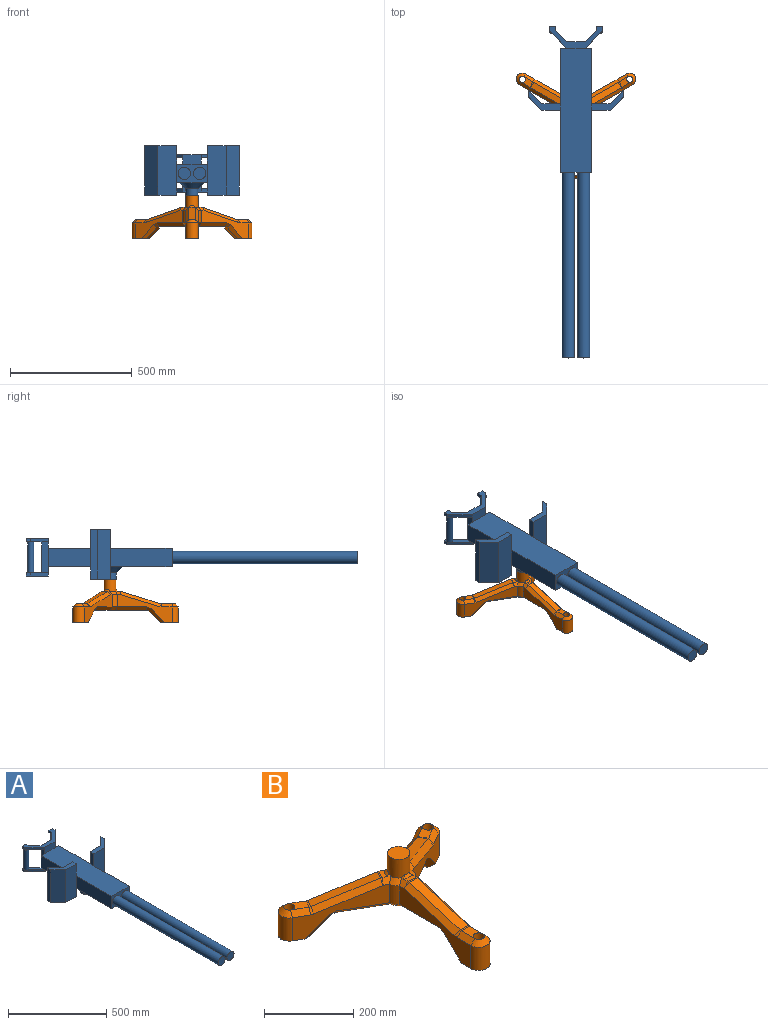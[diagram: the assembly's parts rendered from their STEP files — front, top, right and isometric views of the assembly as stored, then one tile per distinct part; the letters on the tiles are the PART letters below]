
ASSEMBLY  parts=2 mates=1
PART A: 75 faces, bbox 387.2x1360.9x203.2 mm
  f0: cylinder r=25.4mm len=50.8mm, axis (0,0,-1), area 4053.7mm2, adj f18,f74
  f1: plane 71.84x59.14mm, normal (0,0,-1), area 1294.9mm2, adj f3,f44,f45,f57
  f2: plane 71.84x59.14mm, normal (0,0,-1), area 1294.9mm2, adj f4,f42,f43,f54
  f3: plane 127x25.4mm, normal (-1,0,0), area 3225.8mm2, adj f1,f5,f37,f40,f41,f49
  f4: plane 127x25.4mm, normal (1,0,0), area 3225.8mm2, adj f2,f11,f37,f40,f41,f46
  f5: plane 76.2x25.4mm, normal (0,1,0), area 1935.5mm2, adj f3,f6,f7,f8
  f6: plane 508x127mm, normal (0,0,-1), area 56408.7mm2, adj f5,f8,f9,f10,f11,f12,f13,f18
  f7: plane 508x127mm, normal (0,0,1), area 64516mm2, adj f5,f8,f9,f10,f11,f12,f13,f23
  f8: plane 228.6x76.2mm, normal (-1,0,0), area 17419.3mm2, adj f5,f6,f7,f22
  f9: plane 228.6x76.2mm, normal (1,0,0), area 17419.3mm2, adj f6,f7,f11,f20
  f10: plane 254x76.2mm, normal (1,0,0), area 19354.8mm2, adj f6,f7,f13,f19
  f11: plane 76.2x25.4mm, normal (0,1,0), area 1935.5mm2, adj f4,f6,f7,f9
  f12: plane 254x76.2mm, normal (-1,0,0), area 19354.8mm2, adj f6,f7,f13,f21
  f13: plane 127x76.2mm, normal (0,-1,0), area 5623.7mm2, adj f6,f7,f10,f12,f14,f16
  f14: cylinder r=25.4mm len=762mm, axis (0,1,0), area 121609.8mm2, adj f13,f15
  f15: plane 50.8x50.8mm, normal (0,-1,0), area 2026.8mm2, adj f14
  f16: cylinder r=25.4mm len=762mm, axis (0,1,0), area 121609.8mm2, adj f13,f17
  f17: plane 50.8x50.8mm, normal (0,-1,0), area 2026.8mm2, adj f16
  f18: cone r=50.8mm half-angle=45deg, axis (0,0,1), area 8599.1mm2, adj f0,f6
  f19: plane 203.2x76.2mm, normal (0,-1,0), area 15483.8mm2, adj f10,f24,f25,f26,f30,f36
  f20: plane 203.2x76.2mm, normal (0,1,0), area 15483.8mm2, adj f9,f24,f25,f26,f29,f36
  f21: plane 203.2x76.2mm, normal (0,-1,0), area 15483.8mm2, adj f12,f23,f27,f28,f34,f35
  f22: plane 203.2x76.2mm, normal (0,1,0), area 15483.8mm2, adj f8,f23,f27,f28,f32,f35
  f23: plane 76.2x25.4mm, normal (1,0,0), area 1935.5mm2, adj f7,f21,f22,f35
  f24: plane 76.2x25.4mm, normal (-1,0,0), area 1935.5mm2, adj f7,f19,f20,f36
  f25: plane 50.8x25.4mm, normal (-1,0,0), area 1290.3mm2, adj f6,f19,f20,f26
  f26: plane 130.08x79.28mm, normal (0,0,-1), area 3304.1mm2, adj f19,f20,f25,f29,f30,f31
  f27: plane 50.8x25.4mm, normal (1,0,0), area 1290.3mm2, adj f6,f21,f22,f28
  f28: plane 130.08x79.28mm, normal (0,0,-1), area 3304.1mm2, adj f21,f22,f27,f32,f33,f34
  f29: plane 203.2x53.88mm, normal (-0.71,0.71,0), area 15483.8mm2, adj f20,f26,f31,f36
  f30: plane 203.2x53.88mm, normal (0.71,-0.71,0), area 15483.8mm2, adj f19,f26,f31,f36
  f31: plane 203.2x25.4mm, normal (1,0,0), area 5161.3mm2, adj f26,f29,f30,f36
  f32: plane 203.2x53.88mm, normal (0.71,0.71,0), area 15483.8mm2, adj f22,f28,f33,f35
  f33: plane 203.2x25.4mm, normal (-1,0,0), area 5161.3mm2, adj f28,f32,f34,f35
  f34: plane 203.2x53.88mm, normal (-0.71,-0.71,0), area 15483.8mm2, adj f21,f28,f33,f35
  f35: plane 130.08x79.28mm, normal (0,0,1), area 3304.1mm2, adj f21,f22,f23,f32,f33,f34
  f36: plane 130.08x79.28mm, normal (0,0,1), area 3304.1mm2, adj f19,f20,f24,f29,f30,f31
  f37: plane 76.2x38.1mm, normal (0,-1,0), area 2903.2mm2, adj f3,f4,f6,f38,f48,f51
  f38: plane 219.88x90.89mm, normal (0,0,-1), area 5907.6mm2, adj f37,f40,f47,f48,f50,f51,f63,f64
  f39: plane 219.88x90.89mm, normal (0,0,1), area 5907.6mm2, adj f40,f41,f42,f43,f44,f45,f59,f60
  f40: plane 152.4x76.2mm, normal (0,1,0), area 11612.9mm2, adj f3,f4,f38,f39,f43,f45,f47,f50
  f41: plane 76.2x38.1mm, normal (0,-1,0), area 2903.2mm2, adj f3,f4,f7,f39,f42,f44
  f42: plane 71.84x71.84mm, normal (0.71,-0.71,0), area 1290.3mm2, adj f2,f39,f41,f52,f70
  f43: plane 46.44x46.44mm, normal (-0.71,0.71,0), area 834.1mm2, adj f2,f39,f40,f72
  f44: plane 71.84x71.84mm, normal (-0.71,-0.71,0), area 1290.3mm2, adj f1,f39,f41,f55,f60
  f45: plane 46.44x46.44mm, normal (0.71,0.71,0), area 834.1mm2, adj f1,f39,f40,f59
  f46: plane 71.84x59.14mm, normal (0,0,1), area 1294.9mm2, adj f4,f47,f48,f54
  f47: plane 46.44x46.44mm, normal (-0.71,0.71,0), area 834.1mm2, adj f38,f40,f46,f66
  f48: plane 71.84x71.84mm, normal (0.71,-0.71,0), area 1290.3mm2, adj f37,f38,f46,f53,f68
  f49: plane 71.84x59.14mm, normal (0,0,1), area 1294.9mm2, adj f3,f50,f51,f57
  f50: plane 46.44x46.44mm, normal (0.71,0.71,0), area 834.1mm2, adj f38,f40,f49,f64
  f51: plane 71.84x71.84mm, normal (-0.71,-0.71,0), area 1290.3mm2, adj f37,f38,f49,f56,f63
  f52: plane 12.7x12.7mm, normal (0,0,1), area 46mm2, adj f42,f54
  f53: plane 12.7x12.7mm, normal (0,0,-1), area 46mm2, adj f48,f54
  f54: cylinder r=12.7mm len=127mm, axis (0,0,-1), area 10134.1mm2, adj f2,f46,f52,f53,f67,f71
  f55: plane 12.7x12.7mm, normal (0,0,1), area 46mm2, adj f44,f57
  f56: plane 12.7x12.7mm, normal (0,0,-1), area 46mm2, adj f51,f57
  f57: cylinder r=12.7mm len=127mm, axis (0,0,-1), area 10134.1mm2, adj f1,f49,f55,f56,f58,f62
  f58: plane 25.4x19.05mm, normal (0,0,-1), area 230.5mm2, adj f57,f59,f60,f61
  f59: plane 19.05x12.7mm, normal (1,0,0), area 241.9mm2, adj f39,f45,f58,f61
  f60: plane 19.05x12.7mm, normal (-1,0,0), area 241.9mm2, adj f39,f44,f58,f61
  f61: plane 25.4x12.7mm, normal (0,1,0), area 322.6mm2, adj f39,f58,f59,f60
  f62: plane 25.4x19.05mm, normal (0,0,1), area 230.5mm2, adj f57,f63,f64,f65
  f63: plane 19.05x12.7mm, normal (-1,0,0), area 241.9mm2, adj f38,f51,f62,f65
  f64: plane 19.05x12.7mm, normal (1,0,0), area 241.9mm2, adj f38,f50,f62,f65
  f65: plane 25.4x12.7mm, normal (0,1,0), area 322.6mm2, adj f38,f62,f63,f64
  f66: plane 19.05x12.7mm, normal (-1,0,0), area 241.9mm2, adj f38,f47,f67,f69
  f67: plane 25.4x19.05mm, normal (0,0,1), area 230.5mm2, adj f54,f66,f68,f69
  f68: plane 19.05x12.7mm, normal (1,0,0), area 241.9mm2, adj f38,f48,f67,f69
  f69: plane 25.4x12.7mm, normal (0,1,0), area 322.6mm2, adj f38,f66,f67,f68
  f70: plane 19.05x12.7mm, normal (1,0,0), area 241.9mm2, adj f39,f42,f71,f73
  f71: plane 25.4x19.05mm, normal (0,0,-1), area 230.5mm2, adj f54,f70,f72,f73
  f72: plane 19.05x12.7mm, normal (-1,0,0), area 241.9mm2, adj f39,f43,f71,f73
  f73: plane 25.4x12.7mm, normal (0,1,0), area 322.6mm2, adj f39,f70,f71,f72
  f74: plane 50.8x50.8mm, normal (0,0,-1), area 2026.8mm2, adj f0
PART B: 102 faces, bbox 490.9x432x178 mm
  f0: cylinder r=25.4mm len=50.8mm, axis (0,0,-1), area 7731.7mm2, adj f57,f63,f69,f77,f79,f81,f82,f86
  f1: plane 28.72x24.34mm, normal (0,0,1), area 296.1mm2, adj f57,f70,f77,f99
  f2: plane 28.72x24.34mm, normal (0,0,1), area 296.1mm2, adj f69,f76,f81,f98
  f3: plane 195.38x114.3mm, normal (-0.5,0.87,0), area 8864.3mm2, adj f11,f12,f14,f38,f39,f41,f53,f54
  f4: plane 195.38x114.3mm, normal (0.5,0.87,0), area 8864.3mm2, adj f9,f14,f18,f27,f31,f33,f56,f62
  f5: plane 195.38x114.3mm, normal (-0.5,-0.87,0), area 8864.3mm2, adj f9,f15,f18,f23,f24,f25,f66,f72
  f6: plane 225.6x114.3mm, normal (-1,0,0), area 8864.3mm2, adj f10,f13,f15,f29,f30,f32,f89,f90
  f7: plane 195.38x114.3mm, normal (0.5,-0.87,0), area 8864.3mm2, adj f11,f12,f16,f44,f45,f46,f60,f65
  f8: plane 225.6x114.3mm, normal (1,0,0), area 8864.3mm2, adj f10,f13,f16,f35,f37,f40,f80,f82
  f9: cylinder r=25.4mm len=63.5mm, axis (0,0,-1), area 5067.1mm2, adj f4,f5,f18,f61
  f10: cylinder r=25.4mm len=63.5mm, axis (0,0,-1), area 5067.1mm2, adj f6,f8,f13,f85
  f11: cylinder r=25.4mm len=63.5mm, axis (0,0,-1), area 5067.1mm2, adj f3,f7,f12,f55
  f12: plane 73.15x62.32mm, normal (0,0,-1), area 2706.9mm2, adj f3,f7,f11,f21,f38,f46,f97
  f13: plane 73.2x50.8mm, normal (0,0,-1), area 2706.9mm2, adj f6,f8,f10,f20,f30,f35,f96
  f14: cylinder r=38.1mm len=50.8mm, axis (0,0,-1), area 1228.9mm2, adj f3,f4,f36,f63
  f15: cylinder r=38.1mm len=50.8mm, axis (0,0,-1), area 1228.9mm2, adj f5,f6,f26,f86
  f16: cylinder r=38.1mm len=50.8mm, axis (0,0,-1), area 1228.9mm2, adj f7,f8,f42,f79
  f17: plane 25.4x13.44mm, normal (0,0,1), area 296.1mm2, adj f82,f90,f91,f100
  f18: plane 73.15x62.32mm, normal (0,0,-1), area 2706.9mm2, adj f4,f5,f9,f22,f23,f27,f95
  f19: plane 272.75x236.21mm, normal (0,0,-1), area 11615.8mm2, adj f24,f26,f28,f29,f33,f34,f36,f39
  f20: plane 47.08x47.08mm, normal (0,0.71,-0.71), area 1691.2mm2, adj f13,f30,f34,f35
  f21: plane 53.47x47.08mm, normal (-0.61,-0.35,-0.71), area 1691.2mm2, adj f12,f38,f43,f46
  f22: plane 53.47x47.08mm, normal (0.61,-0.35,-0.71), area 1691.2mm2, adj f18,f23,f27,f28
  f23: plane 62.68x56.06mm, normal (0.08,-0.86,-0.5), area 1309.9mm2, adj f5,f18,f22,f25
  f24: plane 117.32x71.87mm, normal (-0.35,-0.61,-0.71), area 2241.6mm2, adj f5,f19,f25,f26
  f25: plane 21.9x16.42mm, normal (-0.1,-0.73,-0.68), area 252.1mm2, adj f5,f23,f24,f28
  f26: cone r=38.1mm half-angle=45deg, axis (0,0,1), area 459mm2, adj f15,f19,f24,f29
  f27: plane 56.06x49.98mm, normal (0.79,0.36,-0.5), area 1309.9mm2, adj f4,f18,f22,f31
  f28: plane 26.49x20.48mm, normal (0.33,-0.19,-0.92), area 246.9mm2, adj f19,f22,f25,f31
  f29: plane 128.14x12.7mm, normal (-0.71,0,-0.71), area 2241.6mm2, adj f6,f19,f26,f32
  f30: plane 65.04x56.06mm, normal (-0.71,0.5,-0.5), area 1309.9mm2, adj f6,f13,f20,f32
  f31: plane 19.98x16.42mm, normal (0.58,0.45,-0.68), area 252.1mm2, adj f4,f27,f28,f33
  f32: plane 17.96x16.42mm, normal (-0.68,0.28,-0.68), area 252.1mm2, adj f6,f29,f30,f34
  f33: plane 111.78x75.07mm, normal (0.35,0.61,-0.71), area 2241.6mm2, adj f4,f19,f31,f36
  f34: plane 25.4x8.98mm, normal (0,0.38,-0.92), area 246.9mm2, adj f19,f20,f32,f37
  f35: plane 65.04x56.06mm, normal (0.71,0.5,-0.5), area 1309.9mm2, adj f8,f13,f20,f37
  f36: cone r=38.1mm half-angle=45deg, axis (0,0,1), area 459mm2, adj f14,f19,f33,f39
  f37: plane 17.96x16.42mm, normal (0.68,0.28,-0.68), area 252.1mm2, adj f8,f34,f35,f40
  f38: plane 56.06x49.98mm, normal (-0.79,0.36,-0.5), area 1309.9mm2, adj f3,f12,f21,f41
  f39: plane 111.78x75.07mm, normal (-0.35,0.61,-0.71), area 2241.6mm2, adj f3,f19,f36,f41
  f40: plane 128.14x12.7mm, normal (0.71,0,-0.71), area 2241.6mm2, adj f8,f19,f37,f42
  f41: plane 19.98x16.42mm, normal (-0.58,0.45,-0.68), area 252.1mm2, adj f3,f38,f39,f43
  f42: cone r=38.1mm half-angle=45deg, axis (0,0,1), area 459mm2, adj f16,f19,f40,f44
  f43: plane 26.49x20.48mm, normal (-0.33,-0.19,-0.92), area 246.9mm2, adj f19,f21,f41,f45
  f44: plane 117.32x71.87mm, normal (0.35,-0.61,-0.71), area 2241.6mm2, adj f7,f19,f42,f45
  f45: plane 21.9x16.42mm, normal (0.1,-0.73,-0.68), area 252.1mm2, adj f7,f43,f44,f46
  f46: plane 62.68x56.06mm, normal (-0.08,-0.86,-0.5), area 1309.9mm2, adj f7,f12,f21,f45
  f47: plane 49.54x43.27mm, normal (0,0,1), area 827.2mm2, adj f56,f66,f67,f95
  f48: plane 49.54x43.27mm, normal (0,0,1), area 827.2mm2, adj f53,f59,f60,f97
  f49: plane 42.54x25.4mm, normal (0,0,1), area 827.2mm2, adj f80,f88,f89,f96
  f50: plane 161.45x49.68mm, normal (0,-0.29,0.96), area 4290.6mm2, adj f83,f88,f91,f94
  f51: plane 152.52x102.72mm, normal (-0.25,0.15,0.96), area 4290.6mm2, adj f67,f68,f75,f76
  f52: plane 152.52x102.72mm, normal (0.25,0.15,0.96), area 4290.6mm2, adj f58,f59,f70,f71
  f53: plane 43.19x32.27mm, normal (-0.35,0.61,0.71), area 764mm2, adj f3,f48,f54,f55
  f54: plane 13.26x12.87mm, normal (-0.26,0.66,0.7), area 101.2mm2, adj f3,f53,f58,f59
  f55: cone r=12.7mm half-angle=45deg, axis (0,0,-1), area 1074.9mm2, adj f11,f53,f60,f97
  f56: plane 43.19x32.27mm, normal (0.35,0.61,0.71), area 764mm2, adj f4,f47,f61,f62
  f57: plane 25.65x19.23mm, normal (-0.35,0.61,0.71), area 340mm2, adj f0,f1,f3,f63,f64,f99
  f58: plane 149.4x89.86mm, normal (-0.17,0.72,0.68), area 3033.9mm2, adj f3,f52,f54,f64
  f59: plane 23.86x15.93mm, normal (0.13,0.07,0.99), area 95.9mm2, adj f48,f52,f54,f65
  f60: plane 43.19x32.27mm, normal (0.35,-0.61,0.71), area 764mm2, adj f7,f48,f55,f65
  f61: cone r=12.7mm half-angle=45deg, axis (0,0,-1), area 1074.9mm2, adj f9,f56,f66,f95
  f62: plane 13.26x12.87mm, normal (0.26,0.66,0.7), area 101.2mm2, adj f4,f56,f67,f68
  f63: cone r=25.4mm half-angle=45deg, axis (0,0,-1), area 459mm2, adj f0,f14,f57,f69
  f64: plane 12.7x11mm, normal (-0.26,0.66,0.7), area 33.7mm2, adj f57,f58,f70
  f65: plane 14.73x13.26mm, normal (0.44,-0.56,0.7), area 101.2mm2, adj f7,f59,f60,f71
  f66: plane 43.19x32.27mm, normal (-0.35,-0.61,0.71), area 764mm2, adj f5,f47,f61,f72
  f67: plane 23.86x15.93mm, normal (-0.13,0.07,0.99), area 95.9mm2, adj f47,f51,f62,f72
  f68: plane 149.4x89.86mm, normal (0.17,0.72,0.68), area 3033.9mm2, adj f4,f51,f62,f73
  f69: plane 25.65x19.23mm, normal (0.35,0.61,0.71), area 340mm2, adj f0,f2,f4,f63,f73,f98
  f70: plane 23.86x15.93mm, normal (0.13,0.07,0.99), area 95.9mm2, adj f1,f52,f64,f74
  f71: plane 142.94x93.59mm, normal (0.53,-0.51,0.68), area 3033.9mm2, adj f7,f52,f65,f74
  f72: plane 14.73x13.26mm, normal (-0.44,-0.56,0.7), area 101.2mm2, adj f5,f66,f67,f75
  f73: plane 12.7x11mm, normal (0.26,0.66,0.7), area 33.7mm2, adj f68,f69,f76
  f74: plane 12.87x12.7mm, normal (0.44,-0.56,0.7), area 33.7mm2, adj f70,f71,f77
  f75: plane 142.94x93.59mm, normal (-0.53,-0.51,0.68), area 3033.9mm2, adj f5,f51,f72,f78
  f76: plane 23.86x15.93mm, normal (-0.13,0.07,0.99), area 95.9mm2, adj f2,f51,f73,f78
  f77: plane 25.24x19.23mm, normal (0.35,-0.61,0.71), area 340mm2, adj f0,f1,f7,f74,f79,f99
  f78: plane 12.87x12.7mm, normal (-0.44,-0.56,0.7), area 33.7mm2, adj f75,f76,f81
  f79: cone r=25.4mm half-angle=45deg, axis (0,0,-1), area 459mm2, adj f0,f16,f77,f82
  f80: plane 42.54x12.7mm, normal (0.71,0,0.71), area 764mm2, adj f8,f49,f84,f85
  f81: plane 25.24x19.23mm, normal (-0.35,-0.61,0.71), area 340mm2, adj f0,f2,f5,f78,f86,f98
  f82: plane 20.72x19.23mm, normal (0.71,0,0.71), area 340mm2, adj f0,f8,f17,f79,f87,f100
  f83: plane 165.18x61.82mm, normal (0.71,-0.21,0.68), area 3033.9mm2, adj f8,f50,f84,f87
  f84: plane 13.26x12.7mm, normal (0.7,-0.11,0.7), area 101.2mm2, adj f8,f80,f83,f88
  f85: cone r=12.7mm half-angle=45deg, axis (0,0,-1), area 1074.9mm2, adj f10,f80,f89,f96
  f86: cone r=25.4mm half-angle=45deg, axis (0,0,-1), area 459mm2, adj f0,f15,f81,f90
  f87: plane 12.7x12.7mm, normal (0.7,-0.11,0.7), area 33.7mm2, adj f82,f83,f91
  f88: plane 25.4x3.74mm, normal (0,-0.15,0.99), area 95.9mm2, adj f49,f50,f84,f92
  f89: plane 42.54x12.7mm, normal (-0.71,0,0.71), area 764mm2, adj f6,f49,f85,f92
  f90: plane 20.72x19.23mm, normal (-0.71,0,0.71), area 340mm2, adj f0,f6,f17,f86,f93,f100
  f91: plane 25.4x3.74mm, normal (0,-0.15,0.99), area 95.9mm2, adj f17,f50,f87,f93
  f92: plane 13.26x12.7mm, normal (-0.7,-0.11,0.7), area 101.2mm2, adj f6,f88,f89,f94
  f93: plane 12.7x12.7mm, normal (-0.7,-0.11,0.7), area 33.7mm2, adj f90,f91,f94
  f94: plane 165.18x61.82mm, normal (-0.71,-0.21,0.68), area 3033.9mm2, adj f6,f50,f92,f93
  f95: cylinder r=12.7mm len=76.2mm, axis (0,0,1), area 6080.5mm2, adj f18,f47,f61
  f96: cylinder r=12.7mm len=76.2mm, axis (0,0,1), area 6080.5mm2, adj f13,f49,f85
  f97: cylinder r=12.7mm len=76.2mm, axis (0,0,1), area 6080.5mm2, adj f12,f48,f55
  f98: cone r=25.4mm half-angle=45deg, axis (0,0,-1), area 174.6mm2, adj f0,f2,f69,f81
  f99: cone r=25.4mm half-angle=45deg, axis (0,0,-1), area 174.6mm2, adj f0,f1,f57,f77
  f100: cone r=25.4mm half-angle=45deg, axis (0,0,-1), area 174.6mm2, adj f0,f17,f82,f90
  f101: plane 50.8x50.8mm, normal (0,0,1), area 2026.8mm2, adj f0
PLACE A t=(0,0,25.4)mm
PLACE B at identity
MATE revolute A.f0 <-> B.f0  axis (0,0,-1) through (0,0,177.8)mm
